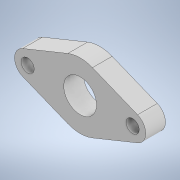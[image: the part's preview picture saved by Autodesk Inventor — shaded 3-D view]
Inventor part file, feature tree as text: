
AUTODESK INVENTOR PART (.ipt)
format: ipt  version: 2022 (Build 260153000, 153)  size: 118,272 bytes
history: native  units: mm
features: other x1, extrude x1, sketch x1
ambient origin geometry x8: Origin, YZ Plane, XZ Plane, XY Plane, X Axis, Y Axis, Z Axis, Center Point
bodies: Body1 (feature_tree)
feature tree (3):
  other  "Sólido1"
  extrude  "Extrusão1"  Depth=10.0mm
  sketch  "Esboço1"  dims[d0=25.0mm d1=10.0mm d2=10.0mm d3=40.0mm d4=80.0mm d5=20.0mm d6=20.0mm d7=50.0mm d8=15.0mm d9=0.0mm]
